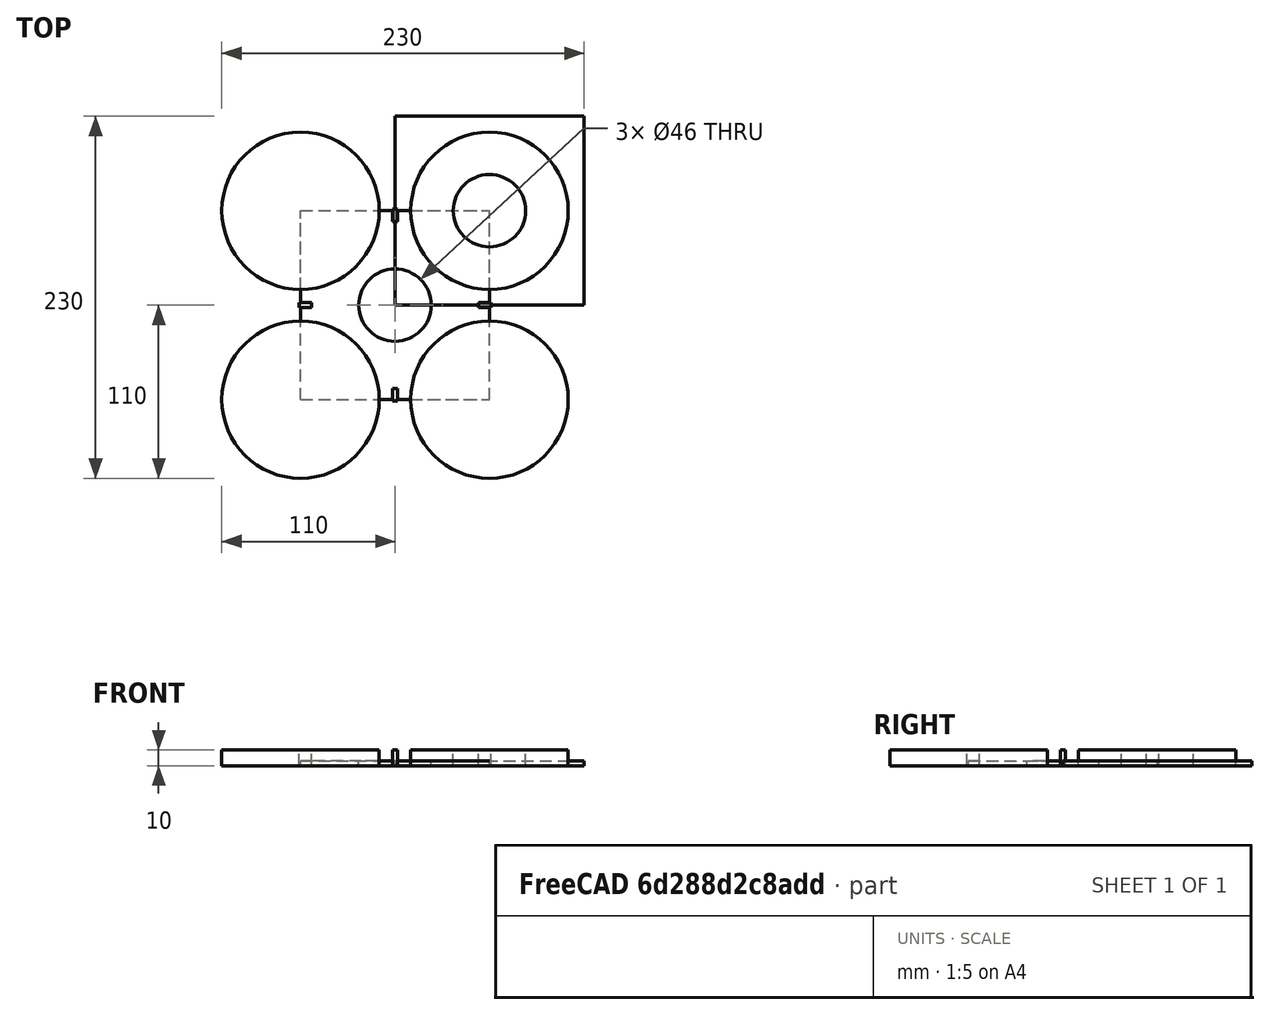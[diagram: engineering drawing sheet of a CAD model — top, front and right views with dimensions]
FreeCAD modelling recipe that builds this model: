
FCSTD DOCUMENT  (FreeCAD 0.14R3702 (Git))
Label: base
License: CC-BY 3.0
LicenseURL: http://creativecommons.org/licenses/by/3.0/
objects: Part::Cut×3, Part::Box×2, Part::Cylinder×2, Part::FeaturePython×2, Part::Part2DObjectPython×1
note: 10 computed .brp shape members not serialized (recipe doc carries the construction recipe); baked Part::Feature solids carry a one-line shape summary decoded from their .brp

FEATURE [Part::Box] Box  label="Cubo"
  Height = 3
  Length = 120
  Width = 120
FEATURE [Part::Cylinder] Cylinder  label="Cilindro"
  Angle = 360
  Height = 10
  Placement = pos=(60,60,0) rot=(0,0,1;0rad)
  Radius = 23
FEATURE [Part::Cut] Cut  label="base"
  Base = -> Box
  Placement = pos=(-60,-60,0) rot=(0,0,1;0rad)
  Tool = -> Cylinder
FEATURE [Part::Cylinder] Cylinder001  label="Cilindro001"
  Angle = 360
  Height = 10
  Placement = pos=(60,60,0) rot=(0,0,1;0rad)
  Radius = 50
FEATURE [Part::FeaturePython] Array  # Draft array (typed FeaturePython)
  Angle = 360
  ArrayType = 1
  Axis = (0,0,1)
  Base = -> Cylinder001
  Center = (0,0,0)
  IntervalX = (1,0,0)
  IntervalY = (0,1,0)
  IntervalZ = (0,0,1)
  NumberPolar = 4
  NumberX = 2
  NumberY = 2
  NumberZ = 1
FEATURE [Part::Cut] Cut001
  Base = -> Cut
  Tool = -> Array
FEATURE [Part::Box] Box001  label="Cubo001"
  Height = 10
  Length = 3.2
  Placement = pos=(-1.6,53,0) rot=(0,0,1;0rad)
  Width = 8
FEATURE [Part::FeaturePython] Array001  # Draft array (typed FeaturePython)
  Angle = 360
  ArrayType = 1
  Axis = (0,0,1)
  Base = -> Box001
  Center = (0,0,0)
  IntervalX = (1,0,0)
  IntervalY = (0,1,0)
  IntervalZ = (0,0,1)
  NumberPolar = 4
  NumberX = 2
  NumberY = 2
  NumberZ = 1
FEATURE [Part::Cut] Cut002
  Base = -> Cut001
  Tool = -> Array001
FEATURE [Part::Part2DObjectPython] Shape2DView  # Draft 2D object (typed FeaturePython)
  Base = -> Cut002
  FaceNumbers = [1]
  HiddenLines = false
  Projection = (0,0,1)
  ProjectionMode = 0
  SegmentLength = 0.05
  Tessellation = false
